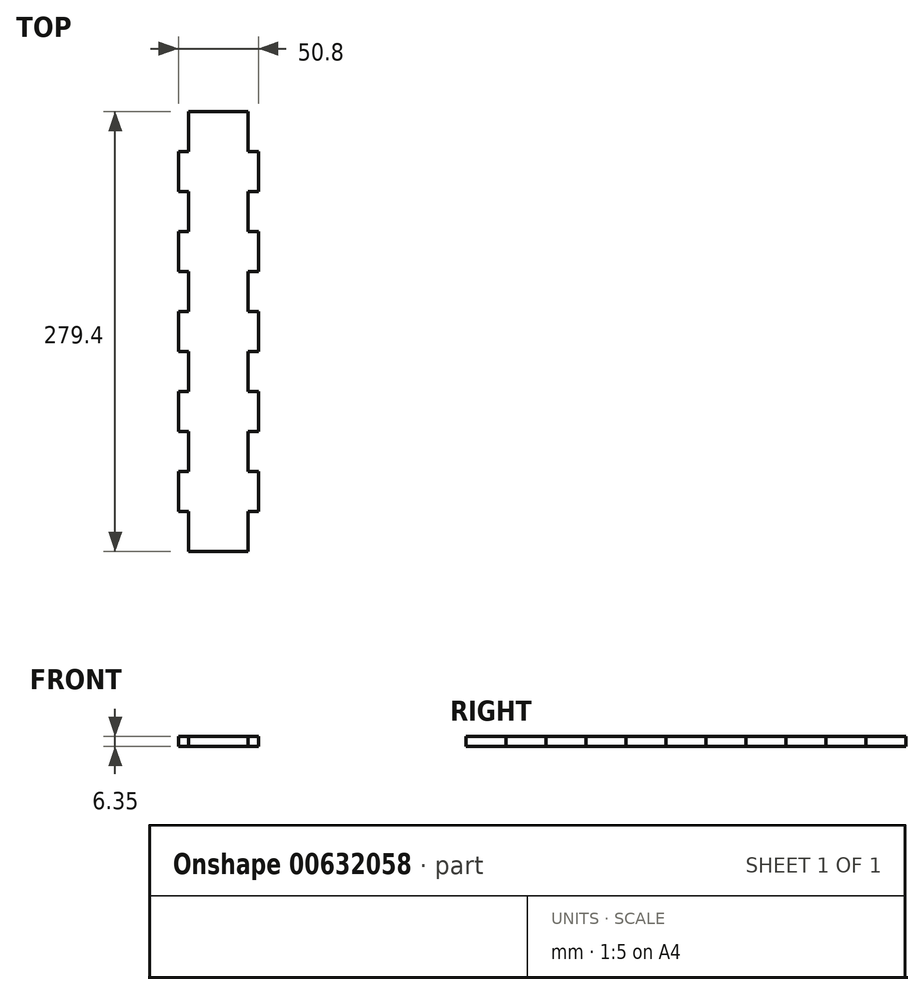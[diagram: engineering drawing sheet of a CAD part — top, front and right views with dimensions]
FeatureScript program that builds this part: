
annotation { "Feature Type Name" : "Feature", "Feature Type Description" : "" }
export const myFeature = defineFeature(function(context is Context, id is Id, definition is map)
    precondition{}
    {
        {
            var Q0;
            Q0=qCreatedBy(makeId("Top.planeOp"),FACE);
            var sketch = newSketch(context, id + "F0", { "sketchPlane" : qUnion([Q0])});
            skLineSegment(sketch, "E0.bottom", {"start": v(0, 279.4) * mm, "end": v(38.1, 279.4) * mm});
            skLineSegment(sketch, "E0.top", {"start": v(0, 0) * mm, "end": v(38.1, 0) * mm});
            skLineSegment(sketch, "E0.left", {"start": v(0, 279.4) * mm, "end": v(0, 0) * mm});
            skLineSegment(sketch, "E0.right", {"start": v(38.1, 279.4) * mm, "end": v(38.1, 0) * mm});
            skSolve(sketch);
        }
        {
            var Q0;
            Q0=qSketchRegion(id+"F0",true);
            extrude(context, id + "F1", {"entities" : qUnion([Q0]), "depth" : 6.35 * mm, "offsetDistance" : 25.4 * mm});
        }
        {
            var Q0;
            Q0=makeQuery(id+"F1.opExtrude","SWEPT_FACE",FACE,{"disambiguationData":[OSD([sQuery(id+"F0.wireOp",EDGE,"E0.right")])]});
            var sketch = newSketch(context, id + "F2", { "sketchPlane" : qUnion([Q0])});
            skLineSegment(sketch, "E1.bottom", {"start": v(0, 6.35) * mm, "end": v(25.4, 6.35) * mm});
            skLineSegment(sketch, "E1.top", {"start": v(0, 0) * mm, "end": v(25.4, 0) * mm});
            skLineSegment(sketch, "E1.left", {"start": v(0, 6.35) * mm, "end": v(0, 0) * mm});
            skLineSegment(sketch, "E1.right", {"start": v(25.4, 6.35) * mm, "end": v(25.4, 0) * mm});
            skLineSegment(sketch, "E2.bottom", {"start": v(25.4, 6.35) * mm, "end": v(50.8, 6.35) * mm});
            skLineSegment(sketch, "E2.top", {"start": v(25.4, 0) * mm, "end": v(50.8, 0) * mm});
            skLineSegment(sketch, "E2.right", {"start": v(50.8, 6.35) * mm, "end": v(50.8, 0) * mm});
            skLineSegment(sketch, "E3.bottom", {"start": v(50.8, 6.35) * mm, "end": v(76.2, 6.35) * mm});
            skLineSegment(sketch, "E3.top", {"start": v(50.8, 0) * mm, "end": v(76.2, 0) * mm});
            skLineSegment(sketch, "E3.right", {"start": v(76.2, 6.35) * mm, "end": v(76.2, 0) * mm});
            skLineSegment(sketch, "E4.bottom", {"start": v(76.2, 6.35) * mm, "end": v(101.6, 6.35) * mm});
            skLineSegment(sketch, "E4.top", {"start": v(76.2, 0) * mm, "end": v(101.6, 0) * mm});
            skLineSegment(sketch, "E4.right", {"start": v(101.6, 6.35) * mm, "end": v(101.6, 0) * mm});
            skLineSegment(sketch, "E5.bottom", {"start": v(101.6, 6.35) * mm, "end": v(127, 6.35) * mm});
            skLineSegment(sketch, "E5.top", {"start": v(101.6, 0) * mm, "end": v(127, 0) * mm});
            skLineSegment(sketch, "E5.right", {"start": v(127, 6.35) * mm, "end": v(127, 0) * mm});
            skLineSegment(sketch, "E6.bottom", {"start": v(127, 6.35) * mm, "end": v(152.4, 6.35) * mm});
            skLineSegment(sketch, "E6.top", {"start": v(127, 0) * mm, "end": v(152.4, 0) * mm});
            skLineSegment(sketch, "E6.right", {"start": v(152.4, 6.35) * mm, "end": v(152.4, 0) * mm});
            skLineSegment(sketch, "E7.bottom", {"start": v(152.4, 6.35) * mm, "end": v(177.8, 6.35) * mm});
            skLineSegment(sketch, "E7.top", {"start": v(152.4, 0) * mm, "end": v(177.8, 0) * mm});
            skLineSegment(sketch, "E7.right", {"start": v(177.8, 6.35) * mm, "end": v(177.8, 0) * mm});
            skLineSegment(sketch, "E8.bottom", {"start": v(177.8, 6.35) * mm, "end": v(203.2, 6.35) * mm});
            skLineSegment(sketch, "E8.top", {"start": v(177.8, 0) * mm, "end": v(203.2, 0) * mm});
            skLineSegment(sketch, "E8.right", {"start": v(203.2, 6.35) * mm, "end": v(203.2, 0) * mm});
            skLineSegment(sketch, "E9.bottom", {"start": v(203.2, 6.35) * mm, "end": v(228.6, 6.35) * mm});
            skLineSegment(sketch, "E9.top", {"start": v(203.2, 0) * mm, "end": v(228.6, 0) * mm});
            skLineSegment(sketch, "E9.right", {"start": v(228.6, 6.35) * mm, "end": v(228.6, 0) * mm});
            skLineSegment(sketch, "E10.bottom", {"start": v(228.6, 6.35) * mm, "end": v(254, 6.35) * mm});
            skLineSegment(sketch, "E10.top", {"start": v(228.6, 0) * mm, "end": v(254, 0) * mm});
            skLineSegment(sketch, "E10.right", {"start": v(254, 6.35) * mm, "end": v(254, 0) * mm});
            skLineSegment(sketch, "E11.bottom", {"start": v(254, 6.35) * mm, "end": v(279.4, 6.35) * mm});
            skLineSegment(sketch, "E11.top", {"start": v(254, 0) * mm, "end": v(279.4, 0) * mm});
            skLineSegment(sketch, "E11.right", {"start": v(279.4, 6.35) * mm, "end": v(279.4, 0) * mm});
            skSolve(sketch);
        }
        {
            var Q0;
            Q0=makeQuery(id+"F1.opExtrude","SWEPT_FACE",FACE,{"disambiguationData":[OSD([sQuery(id+"F0.wireOp",EDGE,"E0.left")])]});
            var sketch = newSketch(context, id + "F3", { "sketchPlane" : qUnion([Q0])});
            skLineSegment(sketch, "E12.bottom", {"start": v(-279.4, 6.35) * mm, "end": v(-254, 6.35) * mm});
            skLineSegment(sketch, "E12.top", {"start": v(-279.4, 0) * mm, "end": v(-254, 0) * mm});
            skLineSegment(sketch, "E12.left", {"start": v(-279.4, 6.35) * mm, "end": v(-279.4, 0) * mm});
            skLineSegment(sketch, "E12.right", {"start": v(-254, 6.35) * mm, "end": v(-254, 0) * mm});
            skLineSegment(sketch, "E13.bottom", {"start": v(-254, 6.35) * mm, "end": v(-228.6, 6.35) * mm});
            skLineSegment(sketch, "E13.top", {"start": v(-254, 0) * mm, "end": v(-228.6, 0) * mm});
            skLineSegment(sketch, "E13.right", {"start": v(-228.6, 6.35) * mm, "end": v(-228.6, 0) * mm});
            skLineSegment(sketch, "E14.bottom", {"start": v(-228.6, 6.35) * mm, "end": v(-203.2, 6.35) * mm});
            skLineSegment(sketch, "E14.top", {"start": v(-228.6, 0) * mm, "end": v(-203.2, 0) * mm});
            skLineSegment(sketch, "E14.right", {"start": v(-203.2, 6.35) * mm, "end": v(-203.2, 0) * mm});
            skLineSegment(sketch, "E15.bottom", {"start": v(-203.2, 6.35) * mm, "end": v(-177.8, 6.35) * mm});
            skLineSegment(sketch, "E15.top", {"start": v(-203.2, 0) * mm, "end": v(-177.8, 0) * mm});
            skLineSegment(sketch, "E15.right", {"start": v(-177.8, 6.35) * mm, "end": v(-177.8, 0) * mm});
            skLineSegment(sketch, "E16.bottom", {"start": v(-177.8, 6.35) * mm, "end": v(-152.4, 6.35) * mm});
            skLineSegment(sketch, "E16.top", {"start": v(-177.8, 0) * mm, "end": v(-152.4, 0) * mm});
            skLineSegment(sketch, "E16.right", {"start": v(-152.4, 6.35) * mm, "end": v(-152.4, 0) * mm});
            skLineSegment(sketch, "E17.bottom", {"start": v(-152.4, 6.35) * mm, "end": v(-127, 6.35) * mm});
            skLineSegment(sketch, "E17.top", {"start": v(-152.4, 0) * mm, "end": v(-127, 0) * mm});
            skLineSegment(sketch, "E17.right", {"start": v(-127, 6.35) * mm, "end": v(-127, 0) * mm});
            skLineSegment(sketch, "E18.bottom", {"start": v(-127, 6.35) * mm, "end": v(-101.6, 6.35) * mm});
            skLineSegment(sketch, "E18.top", {"start": v(-127, 0) * mm, "end": v(-101.6, 0) * mm});
            skLineSegment(sketch, "E18.right", {"start": v(-101.6, 6.35) * mm, "end": v(-101.6, 0) * mm});
            skLineSegment(sketch, "E19.bottom", {"start": v(-101.6, 6.35) * mm, "end": v(-76.2, 6.35) * mm});
            skLineSegment(sketch, "E19.top", {"start": v(-101.6, 0) * mm, "end": v(-76.2, 0) * mm});
            skLineSegment(sketch, "E19.right", {"start": v(-76.2, 6.35) * mm, "end": v(-76.2, 0) * mm});
            skLineSegment(sketch, "E20.bottom", {"start": v(-76.2, 6.35) * mm, "end": v(-50.8, 6.35) * mm});
            skLineSegment(sketch, "E20.top", {"start": v(-76.2, 0) * mm, "end": v(-50.8, 0) * mm});
            skLineSegment(sketch, "E20.right", {"start": v(-50.8, 6.35) * mm, "end": v(-50.8, 0) * mm});
            skLineSegment(sketch, "E21.bottom", {"start": v(-50.8, 6.35) * mm, "end": v(-25.4, 6.35) * mm});
            skLineSegment(sketch, "E21.top", {"start": v(-50.8, 0) * mm, "end": v(-25.4, 0) * mm});
            skLineSegment(sketch, "E21.right", {"start": v(-25.4, 6.35) * mm, "end": v(-25.4, 0) * mm});
            skLineSegment(sketch, "E22.bottom", {"start": v(-25.4, 6.35) * mm, "end": v(0, 6.35) * mm});
            skLineSegment(sketch, "E22.top", {"start": v(-25.4, 0) * mm, "end": v(0, 0) * mm});
            skLineSegment(sketch, "E22.right", {"start": v(0, 6.35) * mm, "end": v(0, 0) * mm});
            skSolve(sketch);
        }
        {
            var Q0;
            Q0=makeQuery(id+"F2.imprint","IMPRINT",FACE,{"disambiguationData":[TD([[makeQuery(id+"F2.imprint","IMPRINT",EDGE,{"derivedFrom":sQuery(id+"F2.wireOp",EDGE,"E10.bottom")}),1.0]])]});
            var Q1;
            Q1=makeQuery(id+"F2.imprint","IMPRINT",FACE,{"disambiguationData":[TD([[makeQuery(id+"F2.imprint","IMPRINT",EDGE,{"derivedFrom":sQuery(id+"F2.wireOp",EDGE,"E8.bottom")}),1.0]])]});
            var Q2;
            Q2=makeQuery(id+"F2.imprint","IMPRINT",FACE,{"disambiguationData":[TD([[makeQuery(id+"F2.imprint","IMPRINT",EDGE,{"derivedFrom":sQuery(id+"F2.wireOp",EDGE,"E6.bottom")}),1.0]])]});
            var Q3;
            Q3=makeQuery(id+"F2.imprint","IMPRINT",FACE,{"disambiguationData":[TD([[makeQuery(id+"F2.imprint","IMPRINT",EDGE,{"derivedFrom":sQuery(id+"F2.wireOp",EDGE,"E4.bottom")}),1.0]])]});
            var Q4;
            Q4=makeQuery(id+"F2.imprint","IMPRINT",FACE,{"disambiguationData":[TD([[makeQuery(id+"F2.imprint","IMPRINT",EDGE,{"derivedFrom":sQuery(id+"F2.wireOp",EDGE,"E2.bottom")}),1.0]])]});
            extrude(context, id + "F4", {"entities" : qUnion([Q0, Q1, Q2, Q3, Q4]), "operationType" : NewBodyOperationType.ADD, "depth" : 6.35 * mm, "offsetDistance" : 25.4 * mm});
        }
        {
            var Q0;
            Q0=makeQuery(id+"F3.imprint","IMPRINT",FACE,{"disambiguationData":[TD([[makeQuery(id+"F3.imprint","IMPRINT",EDGE,{"derivedFrom":sQuery(id+"F3.wireOp",EDGE,"E21.bottom")}),-1.0]])]});
            var Q1;
            Q1=makeQuery(id+"F3.imprint","IMPRINT",FACE,{"disambiguationData":[TD([[makeQuery(id+"F3.imprint","IMPRINT",EDGE,{"derivedFrom":sQuery(id+"F3.wireOp",EDGE,"E19.bottom")}),-1.0]])]});
            var Q2;
            Q2=makeQuery(id+"F3.imprint","IMPRINT",FACE,{"disambiguationData":[TD([[makeQuery(id+"F3.imprint","IMPRINT",EDGE,{"derivedFrom":sQuery(id+"F3.wireOp",EDGE,"E17.bottom")}),-1.0]])]});
            var Q3;
            Q3=makeQuery(id+"F3.imprint","IMPRINT",FACE,{"disambiguationData":[TD([[makeQuery(id+"F3.imprint","IMPRINT",EDGE,{"derivedFrom":sQuery(id+"F3.wireOp",EDGE,"E15.bottom")}),-1.0]])]});
            var Q4;
            Q4=makeQuery(id+"F3.imprint","IMPRINT",FACE,{"disambiguationData":[TD([[makeQuery(id+"F3.imprint","IMPRINT",EDGE,{"derivedFrom":sQuery(id+"F3.wireOp",EDGE,"E13.bottom")}),-1.0]])]});
            extrude(context, id + "F5", {"entities" : qUnion([Q0, Q1, Q2, Q3, Q4]), "operationType" : NewBodyOperationType.ADD, "depth" : 6.35 * mm, "offsetDistance" : 25.4 * mm});
        }
    });
